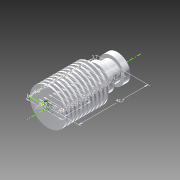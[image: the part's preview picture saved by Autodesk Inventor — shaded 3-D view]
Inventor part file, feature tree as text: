
AUTODESK INVENTOR PART (.ipt)
format: ipt  version: 2015 (Build 190159000, 159)  size: 479,232 bytes
history: native  units: mm
features: sketch x3, hole x3, other x2, revolve x1
ambient origin geometry x8: Origin, YZ Plane, XZ Plane, XY Plane, X Axis, Y Axis, Z Axis, Center Point
bodies: Body1 (feature_tree)
feature tree (9):
  other  "Твердое тело1"
  sketch  "Эскиз1"
  revolve  "Вращение1"
  sketch  "Эскиз2"
  hole  "Отверстие1"  [1 undecoded]
  hole  "Отверстие3"  [1 undecoded]
  hole  "Отверстие4"  [1 undecoded]
  other  "Пружина3"
  sketch  "Эскиз3"
note: 3 required parameter values undecoded (feature->parameter linkage not recoverable at this tier; creation-order binding heuristic only, values carry confidence <= 0.55)
